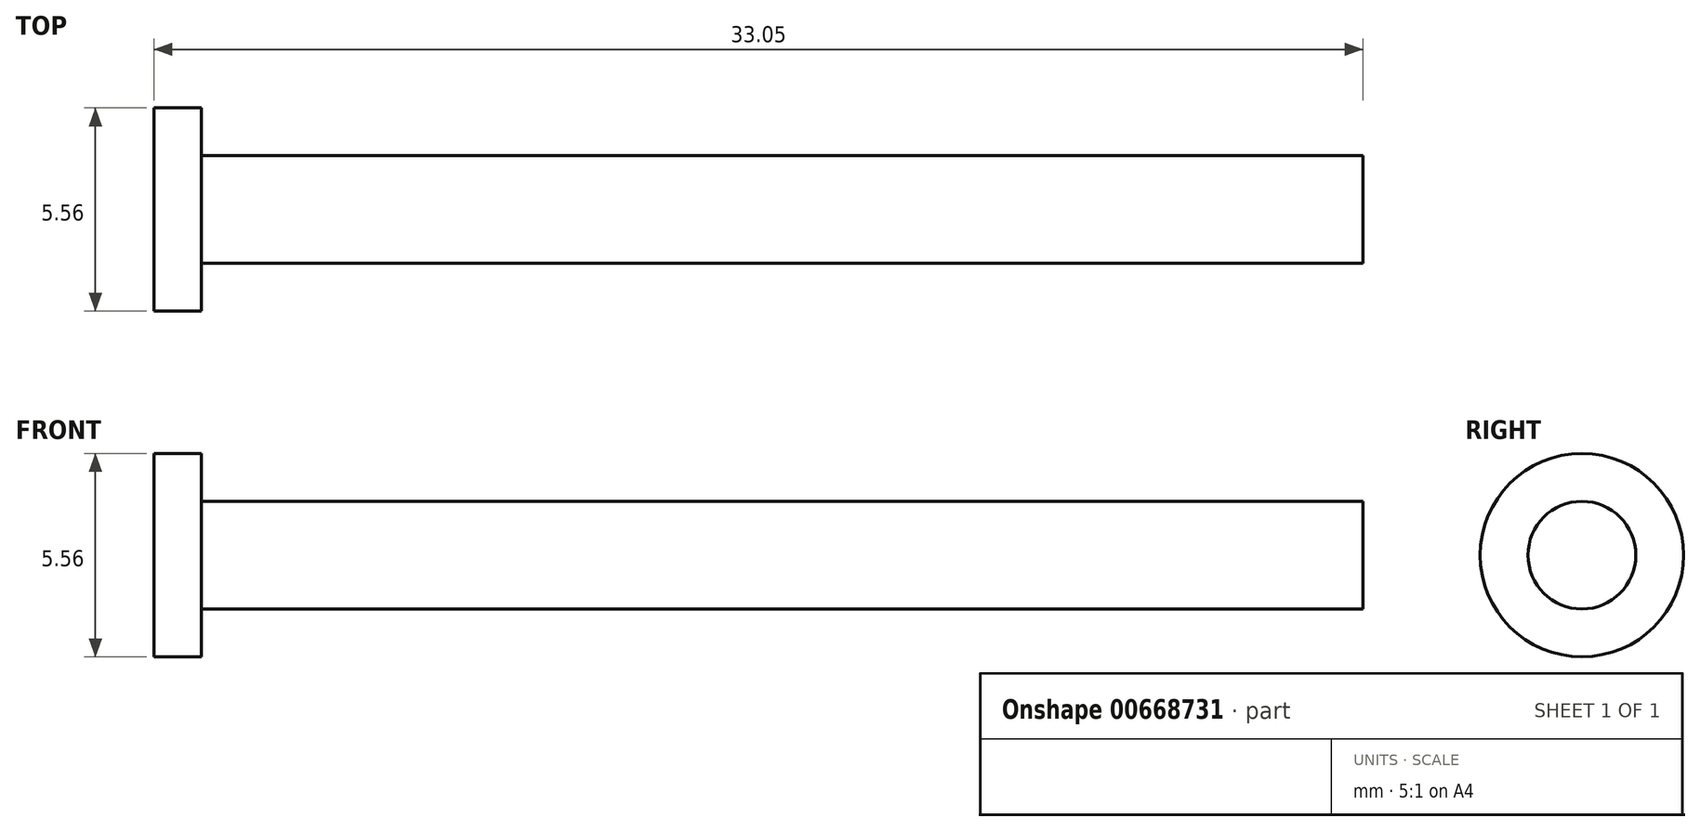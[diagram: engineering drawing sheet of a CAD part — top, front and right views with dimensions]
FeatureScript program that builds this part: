
annotation { "Feature Type Name" : "Feature", "Feature Type Description" : "" }
export const myFeature = defineFeature(function(context is Context, id is Id, definition is map)
    precondition{}
    {
        {
            var Q0;
            Q0=qCreatedBy(makeId("Top.planeOp"),FACE);
            var sketch = newSketch(context, id + "F0", { "sketchPlane" : qUnion([Q0])});
            skLineSegment(sketch, "E0.bottom", {"start": v(0, 0) * mm, "end": v(-1.3, 0) * mm});
            skLineSegment(sketch, "E0.top", {"start": v(0, 2.78) * mm, "end": v(-1.3, 2.78) * mm});
            skLineSegment(sketch, "E0.left", {"start": v(0, 0) * mm, "end": v(0, 2.78) * mm});
            skLineSegment(sketch, "E0.right", {"start": v(-1.3, 0) * mm, "end": v(-1.3, 2.78) * mm});
            skLineSegment(sketch, "E1.bottom", {"start": v(0, 0) * mm, "end": v(31.75, 0) * mm});
            skLineSegment(sketch, "E1.top", {"start": v(0, 1.47) * mm, "end": v(31.75, 1.47) * mm});
            skLineSegment(sketch, "E1.left", {"start": v(0, 0) * mm, "end": v(0, 1.47) * mm});
            skLineSegment(sketch, "E1.right", {"start": v(31.75, 0) * mm, "end": v(31.75, 1.47) * mm});
            skSolve(sketch);
        }
        {
            var Q0;
            Q0=makeQuery(id+"F0.imprint","IMPRINT",FACE,{"disambiguationData":[TD([[makeQuery(id+"F0.imprint","IMPRINT",EDGE,{"derivedFrom":sQuery(id+"F0.wireOp",EDGE,"E0.bottom")}),-1.0]])]});
            var Q1;
            Q1=makeQuery(id+"F0.imprint","IMPRINT",FACE,{"disambiguationData":[TD([[makeQuery(id+"F0.imprint","IMPRINT",EDGE,{"derivedFrom":sQuery(id+"F0.wireOp",EDGE,"E1.bottom")}),1.0]])]});
            var Q2;
            Q2=sQuery(id+"F0.wireOp",EDGE,"E1.bottom");
            revolve(context, id + "F1", {"surfaceOperationType" : NewSurfaceOperationType.NEW, "entities" : qUnion([Q0, Q1]), "axis" : qUnion([Q2]), "revolveType" : RevolveType.FULL});
        }
    });
